# Revit family: Bed_Malvestio_348650
name_source: partatom
category: Furniture
revit_build: Autodesk Revit Architecture 2014 (Build: 20131024_2115(x64)
units: mm (PartAtom-declared; Revit-internal decimal feet)

## types (1)
- Bed_Malvestio_348650
    BIMobject category = Other Furniture
    Date of publishing = 2014-10-30
    Depth = 970 mm  [stored 3.18241 ft]
    Description = Electric bed, pediatric, adjustable height on two columns, with trend, reverse trend, and electrically operated bed lengthener from cm 155 to cm 195
    Design country = Italy
    Edition number = 1
    Height = 1252 mm
    IFC Classification = Furniture
    Installation instructions = http://www.malvestio.it
    Manufacturer URL = http://www.malvestio.it
    Manufacturer country = Italy
    Manufacturer name = Malvestio
    Material Main = Bed_MalvestioPAEDIATRICS 348650_White
    Nominal height = 970
    Nominal width = 1950
    Product SKU = PAEDIATRICS-348650
    Product data url = http://www.malvestio.it
    QR code = http://malvestio.bimobject.com
    UNSPSC Code = 56
    Weight Net (Kg) = 0
    Width = 1793 mm  [stored 5.88255 ft]
    Youtube clip = http://www.malvestio.it

note: [stored X ft] marks values corroborated as IEEE doubles in the binary element streams (Revit-internal decimal feet)

## geometry (parser evidence)
native form markers: Sweep x3
no freeform markers — native parametric forms only
